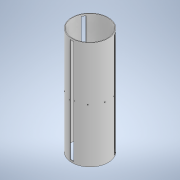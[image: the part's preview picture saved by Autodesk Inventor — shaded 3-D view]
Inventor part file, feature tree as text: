
AUTODESK INVENTOR PART (.ipt)
format: ipt  version: 2021 (Build 250183000, 183)  size: 258,048 bytes
history: native  units: in
note: dims shown in document units (in); Inventor stores cm internally (conversion verified against a paired STEP export)
features: other x28, hole x7, pattern_circular x6, sketch x6, plane x5, extrude x2
ambient origin geometry x8: Origin, YZ Plane, XZ Plane, XY Plane, X Axis, Y Axis, Z Axis, Center Point
bodies: Solid1 (feature_tree)
feature tree (54):
  extrude  "Extrusion1"  Depth=0.3937in
  plane  "Work Plane1"
  extrude  "Extrusion2"  Depth=0.3937in TaperAngle=0.0deg
  pattern_circular  "Circular Pattern1"  Count=3 Angle=360.0deg
  other  "Work Axis1"
  other  "Work Axis2"
  other  "Work Axis3"
  other  "Work Axis4"
  other  "Work Point1"
  other  "Work Point2"
  other  "Work Point3"
  other  "Central Plane"
  other  "Work Point4"
  other  "Work Axis6"
  other  "Work Axis7"
  other  "Offset Plane A"
  other  "Work Point5"
  other  "Work Point6"
  other  "Work Axis8"
  other  "Work Axis9"
  other  "Work Point7"
  other  "Work Point8"
  plane  "Work Plane5"
  plane  "Work Plane6"
  hole  "Hole1"  [1 undecoded]
  hole  "Hole2"  [1 undecoded]
  pattern_circular  "Circular Pattern3"  Count=3 Angle=360.0deg
  sketch  "Sketch5"  dims[d13=0.0484in d14=-11.811in]
  plane  "Work Plane7"
  sketch  "Sketch6"  dims[d15=0.0484in d16=0.1574in]
  hole  "Hole3"  [1 undecoded]
  other  "Work Axis10"
  hole  "Hole4"  [1 undecoded]
  pattern_circular  "Circular Pattern5"  Count=4 Angle=360.0deg
  plane  "Work Plane12"
  hole  "Hole5"  [1 undecoded]
  pattern_circular  "Circular Pattern6"  Count=3 Angle=360.0deg
  other  "plane for insert hole 1"
  sketch  "Sketch7"  dims[d17=-0.1574in]
  other  "plane for insert hole 2"
  hole  "insert hole 2"  [1 undecoded]
  hole  "insert hole 1"  [1 undecoded]
  pattern_circular  "Circular Pattern7"  [2 undecoded]
  pattern_circular  "Circular Pattern9"  [2 undecoded]
  sketch  "Sketch1"  dims[d3=0.0in d5=0.3937in]
  sketch  "Sketch2"  dims[d7=0.3937in d8=0.5in d9=0.0in d10=1.1811in d11=360.0deg]
  other  "Work Axis5"
  other  "Offset Plane B"
  other  "Work Axis11"
  other  "Work Axis12"
  other  "Work Point9"
  other  "Work Axis13"
  other  "Work Point10"
  sketch  "Sketch8"  dims[d48=1.0in d49=1.0in d29=0.096in d30=0.75in d31=0.185in d32=0.25in d33=0.5635in d34=1.0in d35=0.0in d52=1.0in d53=1.0in d38=0.096in d39=0.75in d40=0.185in d41=0.25in d42=0.5635in d43=1.0in d44=0.8108in d45=1.1811in d46=360.0deg d51=0.38in d54=0.177in d55=0.328in d56=0.332in d57=0.25in d58=0.5635in d59=0.484in d60=0.8108in d64=0.19in d65=0.177in d66=0.3229in d67=0.332in d68=0.25in d69=0.5635in d70=0.484in d71=0.8108in d72=1.5748in d73=360.0deg d75=60.0deg d76=1.0in d77=1.0in d78=0.129in d79=0.3229in d80=0.225in d81=0.25in d82=0.5635in d83=0.484in d84=0.8108in d85=1.1811in d86=360.0deg d88=0.2749in d89=0.2749in d90=0.0in d91=0.0in d92=0.0in d93=11.811in d94=0.0in d95=11.811in d96=0.129in d97=0.224in d98=0.225in d99=0.25in d100=0.5635in d101=0.349in d102=0.8108in d103=0.129in d104=0.224in d105=0.225in d106=0.25in d107=0.5635in d108=0.349in d109=0.8108in d110=1.1811in d111=360.0deg d116=1.1811in d117=360.0deg d119=0.0in d61=0.75in d62=0.8108in d63=0.0625in]
note: 11 required parameter values undecoded (feature->parameter linkage not recoverable at this tier; creation-order binding heuristic only, values carry confidence <= 0.55)
